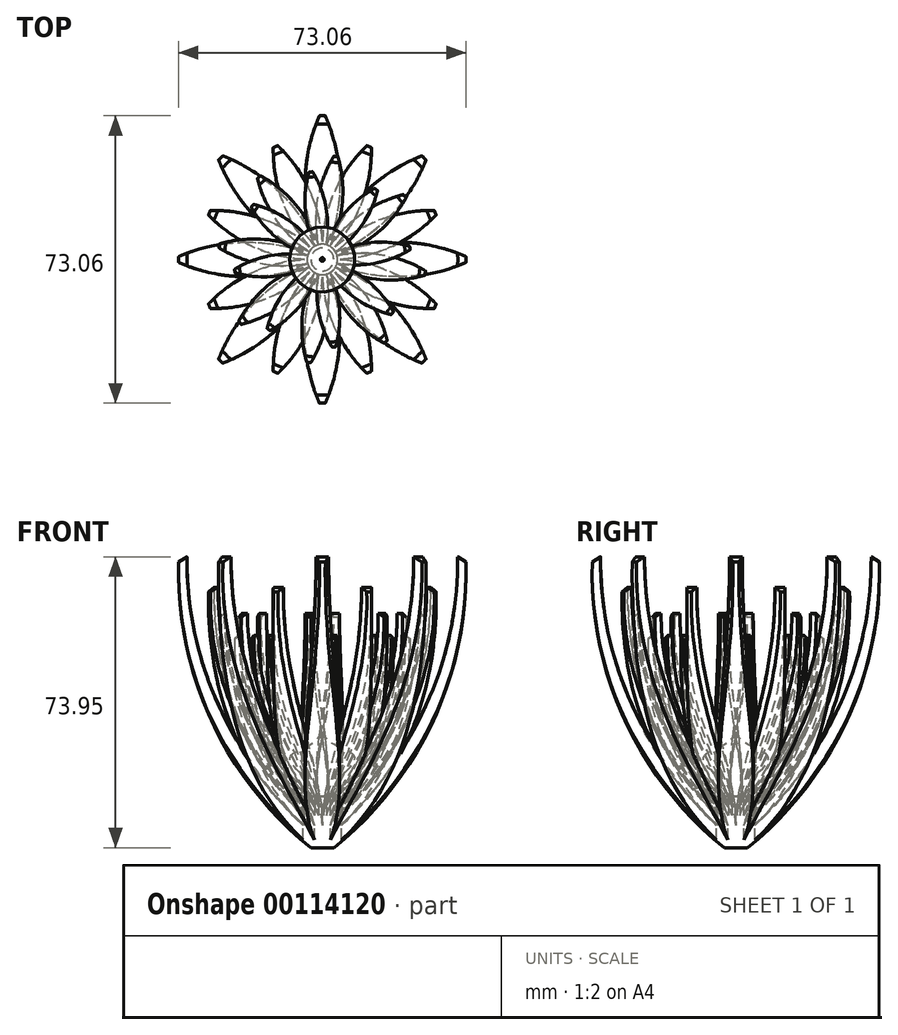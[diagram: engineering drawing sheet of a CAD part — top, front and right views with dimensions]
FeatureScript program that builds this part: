
annotation { "Feature Type Name" : "Feature", "Feature Type Description" : "" }
export const myFeature = defineFeature(function(context is Context, id is Id, definition is map)
    precondition{}
    {
        {
            var Q0;
            Q0=qCreatedBy(makeId("Top.planeOp"),FACE);
            var sketch = newSketch(context, id + "F0", { "sketchPlane" : qUnion([Q0])});
            skLineSegment(sketch, "E0.bottom", {"start": v(38.1, -38.1) * mm, "end": v(-38.1, -38.1) * mm});
            skLineSegment(sketch, "E0.top", {"start": v(38.1, 38.1) * mm, "end": v(-38.1, 38.1) * mm});
            skLineSegment(sketch, "E0.left", {"start": v(38.1, -38.1) * mm, "end": v(38.1, 38.1) * mm});
            skLineSegment(sketch, "E0.right", {"start": v(-38.1, -38.1) * mm, "end": v(-38.1, 38.1) * mm});
            skPoint(sketch, "E0.middle", {"position": v(0, 0) * mm});
            skSolve(sketch);
        }
        {
            var Q0;
            Q0=qSketchRegion(id+"F0",true);
            extrude(context, id + "F1", {"entities" : qUnion([Q0]), "depth" : 76.2 * mm});
        }
        {
            var Q0;
            Q0=makeQuery(id+"F1.opExtrude","CAP_FACE",FACE,{"disambiguationData":[OSD([sQuery(id+"F0.wireOp",EDGE,"E0.bottom"),sQuery(id+"F0.wireOp",EDGE,"E0.top"),sQuery(id+"F0.wireOp",EDGE,"E0.left"),sQuery(id+"F0.wireOp",EDGE,"E0.right")])],"isStart":false});
            var sketch = newSketch(context, id + "F2", { "sketchPlane" : qUnion([Q0])});
            skCircle(sketch, "E1", {"center": v(0, 0) * mm, "radius": 3.18 * mm, "construction": true});
            skLineSegment(sketch, "E2", {"start": v(-38.1, 38.1) * mm, "end": v(38.1, -38.1) * mm, "construction": true});
            skLineSegment(sketch, "E3", {"start": v(38.1, 38.1) * mm, "end": v(-38.1, -38.1) * mm, "construction": true});
            skLineSegment(sketch, "E4", {"start": v(0, -38.1) * mm, "end": v(0, 38.1) * mm, "construction": true});
            skLineSegment(sketch, "E5", {"start": v(-38.1, 0) * mm, "end": v(38.1, 0) * mm, "construction": true});
            skLineSegment(sketch, "E6.bottom", {"start": v(-38.1, 38.1) * mm, "end": v(38.1, 38.1) * mm});
            skLineSegment(sketch, "E6.top", {"start": v(-38.1, -38.1) * mm, "end": v(38.1, -38.1) * mm});
            skLineSegment(sketch, "E6.left", {"start": v(-38.1, 38.1) * mm, "end": v(-38.1, -38.1) * mm});
            skLineSegment(sketch, "E6.right", {"start": v(38.1, 38.1) * mm, "end": v(38.1, -38.1) * mm});
            skArc(sketch, "E7", {"start": v(0, 0) * mm, "mid": v(4.4, 19.05) * mm, "end": v(0, 38.1) * mm});
            skArc(sketch, "E8.MirrorCS", {"start": v(0, 0) * mm, "mid": v(-4.4, 19.05) * mm, "end": v(0, 38.1) * mm});
            skArc(sketch, "E9.1.0", {"start": v(0, 0) * mm, "mid": v(-10.36, 16.58) * mm, "end": v(-26.94, 26.94) * mm});
            skArc(sketch, "E9.1.1", {"start": v(0, 0) * mm, "mid": v(-16.58, 10.36) * mm, "end": v(-26.94, 26.94) * mm});
            skArc(sketch, "E9.2.0", {"start": v(0, 0) * mm, "mid": v(-19.05, 4.4) * mm, "end": v(-38.1, 0) * mm});
            skArc(sketch, "E9.2.1", {"start": v(0, 0) * mm, "mid": v(-19.05, -4.4) * mm, "end": v(-38.1, 0) * mm});
            skArc(sketch, "E9.3.0", {"start": v(0, 0) * mm, "mid": v(-16.58, -10.36) * mm, "end": v(-26.94, -26.94) * mm});
            skArc(sketch, "E9.3.1", {"start": v(0, 0) * mm, "mid": v(-10.36, -16.58) * mm, "end": v(-26.94, -26.94) * mm});
            skArc(sketch, "E9.4.0", {"start": v(0, 0) * mm, "mid": v(-4.4, -19.05) * mm, "end": v(0, -38.1) * mm});
            skArc(sketch, "E9.4.1", {"start": v(0, 0) * mm, "mid": v(4.4, -19.05) * mm, "end": v(0, -38.1) * mm});
            skArc(sketch, "E9.5.0", {"start": v(0, 0) * mm, "mid": v(10.36, -16.58) * mm, "end": v(26.94, -26.94) * mm});
            skArc(sketch, "E9.5.1", {"start": v(0, 0) * mm, "mid": v(16.58, -10.36) * mm, "end": v(26.94, -26.94) * mm});
            skArc(sketch, "E9.6.0", {"start": v(0, 0) * mm, "mid": v(19.05, -4.4) * mm, "end": v(38.1, 0) * mm});
            skArc(sketch, "E9.6.1", {"start": v(0, 0) * mm, "mid": v(19.05, 4.4) * mm, "end": v(38.1, 0) * mm});
            skArc(sketch, "E9.7.0", {"start": v(0, 0) * mm, "mid": v(16.58, 10.36) * mm, "end": v(26.94, 26.94) * mm});
            skArc(sketch, "E9.7.1", {"start": v(0, 0) * mm, "mid": v(10.36, 16.58) * mm, "end": v(26.94, 26.94) * mm});
            skSolve(sketch);
        }
        {
            var Q0;
            {var subQ0=sQuery(id+"F2.wireOp",EDGE,"E9.1.1");var subQ1=sQuery(id+"F2.wireOp",EDGE,"E9.1.0");var subQ2=makeQuery(id+"F2.imprint","INTERSECT",VERTEX,{"derivedFrom":[subQ1,subQ0]});Q0=makeQuery(id+"F2.imprint","IMPRINT",FACE,{"disambiguationData":[TD([[makeQuery(id+"F2.imprint","IMPRINT",EDGE,{"disambiguationData":[TD([[subQ2,1.0]])],"derivedFrom":subQ1}),-1.0]])]});}
            var Q1;
            {var subQ0=sQuery(id+"F2.wireOp",EDGE,"E9.5.1");var subQ1=sQuery(id+"F2.wireOp",EDGE,"E9.5.0");var subQ2=makeQuery(id+"F2.imprint","INTERSECT",VERTEX,{"derivedFrom":[subQ1,subQ0]});Q1=makeQuery(id+"F2.imprint","IMPRINT",FACE,{"disambiguationData":[TD([[makeQuery(id+"F2.imprint","IMPRINT",EDGE,{"disambiguationData":[TD([[subQ2,1.0]])],"derivedFrom":subQ1}),-1.0]])]});}
            var Q2;
            {var subQ0=sQuery(id+"F2.wireOp",EDGE,"E9.3.1");var subQ1=sQuery(id+"F2.wireOp",EDGE,"E9.3.0");var subQ2=makeQuery(id+"F2.imprint","INTERSECT",VERTEX,{"derivedFrom":[subQ1,subQ0]});Q2=makeQuery(id+"F2.imprint","IMPRINT",FACE,{"disambiguationData":[TD([[makeQuery(id+"F2.imprint","IMPRINT",EDGE,{"disambiguationData":[TD([[subQ2,1.0]])],"derivedFrom":subQ1}),-1.0]])]});}
            var Q3;
            {var subQ3=sQuery(id+"F2.wireOp",EDGE,"E9.7.0");var subQ9=sQuery(id+"F2.wireOp",EDGE,"E9.7.1");var subQ11=makeQuery(id+"F2.imprint","INTERSECT",VERTEX,{"derivedFrom":[subQ3,subQ9]});Q3=makeQuery(id+"F2.imprint","IMPRINT",FACE,{"disambiguationData":[TD([[makeQuery(id+"F2.imprint","IMPRINT",EDGE,{"disambiguationData":[TD([[subQ11,1.0]])],"derivedFrom":subQ3}),-1.0]])]});}
            extrude(context, id + "F3", {"entities" : qUnion([Q0, Q1, Q2, Q3]), "operationType" : NewBodyOperationType.REMOVE, "endBound" : BoundingType.THROUGH_ALL, "oppositeDirection" : true, "depth" : 25.4 * mm});
        }
        {
            var Q0;
            Q0=qCreatedBy(makeId("Front.planeOp"),FACE);
            var sketch = newSketch(context, id + "F4", { "sketchPlane" : qUnion([Q0])});
            skLineSegment(sketch, "E10", {"start": v(0, 0) * mm, "end": v(0, 59.45) * mm, "construction": true});
            skPoint(sketch, "E11.0", {"position": v(-38.1, 76.2) * mm});
            skPoint(sketch, "E11.1", {"position": v(38.1, 76.2) * mm});
            skPoint(sketch, "E11.2", {"position": v(38.1, 0) * mm});
            skPoint(sketch, "E11.3", {"position": v(-38.1, 0) * mm});
            skLineSegment(sketch, "E12.bottom", {"start": v(-38.1, 76.2) * mm, "end": v(38.1, 76.2) * mm, "construction": true});
            skLineSegment(sketch, "E12.top", {"start": v(-38.1, 0) * mm, "end": v(38.1, 0) * mm, "construction": true});
            skLineSegment(sketch, "E12.left", {"start": v(-38.1, 76.2) * mm, "end": v(-38.1, 0) * mm, "construction": true});
            skLineSegment(sketch, "E12.right", {"start": v(38.1, 76.2) * mm, "end": v(38.1, 0) * mm, "construction": true});
            skArc(sketch, "E13", {"start": v(-34.42, 76.2) * mm, "mid": v(-25.55, 36.17) * mm, "end": v(0, 4.1) * mm});
            skArc(sketch, "E14", {"start": v(-36.5, 74.86) * mm, "mid": v(-27.42, 32.96) * mm, "end": v(0, 0) * mm});
            skLineSegment(sketch, "E15.bottom", {"start": v(0, 86.56) * mm, "end": v(-47.12, 86.56) * mm});
            skLineSegment(sketch, "E15.top", {"start": v(0, -8.54) * mm, "end": v(-47.12, -8.54) * mm});
            skLineSegment(sketch, "E15.left", {"start": v(0, 86.56) * mm, "end": v(0, -8.54) * mm});
            skLineSegment(sketch, "E15.right", {"start": v(-47.12, 86.56) * mm, "end": v(-47.12, -8.54) * mm});
            skLineSegment(sketch, "E16", {"start": v(-34.42, 76.2) * mm, "end": v(-36.5, 74.86) * mm});
            skLineSegment(sketch, "E17", {"start": v(0, 4.1) * mm, "end": v(0, 0) * mm});
            skSolve(sketch);
        }
        {
            var Q0;
            {var subQ4=sQuery(id+"F4.wireOp",EDGE,"E13");Q0=makeQuery(id+"F4.imprint","IMPRINT",FACE,{"disambiguationData":[TD([[makeQuery(id+"F4.imprint","IMPRINT",EDGE,{"derivedFrom":subQ4}),1.0]])]});}
            var Q1;
            Q1=sQuery(id+"F4.wireOp",EDGE,"E15.left");
            revolve(context, id + "F5", {"operationType" : NewBodyOperationType.REMOVE, "entities" : qUnion([Q0]), "axis" : qUnion([Q1]), "revolveType" : RevolveType.FULL, "oppositeDirection" : true});
        }
        {
            var Q0;
            Q0=qCreatedBy(makeId("Front.planeOp"),FACE);
            var sketch = newSketch(context, id + "F6", { "sketchPlane" : qUnion([Q0])});
            skLineSegment(sketch, "E18", {"start": v(0, 0) * mm, "end": v(0, 66.84) * mm, "construction": true});
            skSolve(sketch);
        }
        {
            var Q0;
            Q0=makeQuery(id+"F1.opExtrude","SWEPT_BODY",BODY,{"disambiguationData":[OSD([sQuery(id+"F0.wireOp",EDGE,"E0.bottom"),sQuery(id+"F0.wireOp",EDGE,"E0.top"),sQuery(id+"F0.wireOp",EDGE,"E0.left"),sQuery(id+"F0.wireOp",EDGE,"E0.right")])]});
            transform(context, id + "F7", {"entities" : qUnion([Q0]), "transformType" : TransformType.TRANSLATION_3D, "dx" : 0 * mm, "dy" : 0 * mm, "dz" : 4.32 * mm, "makeCopy" : true});
        }
        {
            var Q0;
            Q0=makeQuery(id+"F7.opPattern","COPY",BODY,{"derivedFrom":makeQuery(id+"F1.opExtrude","SWEPT_BODY",BODY,{"disambiguationData":[OSD([sQuery(id+"F0.wireOp",EDGE,"E0.bottom"),sQuery(id+"F0.wireOp",EDGE,"E0.top"),sQuery(id+"F0.wireOp",EDGE,"E0.left"),sQuery(id+"F0.wireOp",EDGE,"E0.right")])]}),"instanceName":"1"});
            var Q1;
            Q1=sQuery(id+"F6.wireOp",EDGE,"E18");
            transform(context, id + "F8", {"entities" : qUnion([Q0]), "transformType" : TransformType.ROTATION, "transformAxis" : qUnion([Q1]), "angle" : 22.5 * degree, "makeCopy" : false});
        }
        {
            var Q0;
            Q0=makeQuery(id+"F7.opPattern","COPY",BODY,{"derivedFrom":makeQuery(id+"F1.opExtrude","SWEPT_BODY",BODY,{"disambiguationData":[OSD([sQuery(id+"F0.wireOp",EDGE,"E0.bottom"),sQuery(id+"F0.wireOp",EDGE,"E0.top"),sQuery(id+"F0.wireOp",EDGE,"E0.left"),sQuery(id+"F0.wireOp",EDGE,"E0.right")])]}),"instanceName":"1"});
            var Q1;
            Q1=qCreatedBy(makeId("Origin.pointOp"),VERTEX);
            transform(context, id + "F9", {"entities" : qUnion([Q0]), "transformType" : TransformType.SCALE_UNIFORMLY, "scale" : .85, "scalePoint" : qUnion([Q1]), "makeCopy" : false});
        }
        {
            var Q0;
            Q0=makeQuery(id+"F7.opPattern","COPY",BODY,{"derivedFrom":makeQuery(id+"F1.opExtrude","SWEPT_BODY",BODY,{"disambiguationData":[OSD([sQuery(id+"F0.wireOp",EDGE,"E0.bottom"),sQuery(id+"F0.wireOp",EDGE,"E0.top"),sQuery(id+"F0.wireOp",EDGE,"E0.left"),sQuery(id+"F0.wireOp",EDGE,"E0.right")])]}),"instanceName":"1"});
            transform(context, id + "F10", {"entities" : qUnion([Q0]), "transformType" : TransformType.TRANSLATION_3D, "dx" : 0 * mm, "dy" : 0 * mm, "dz" : 4.32 * mm, "makeCopy" : true});
        }
        {
            var Q0;
            Q0=makeQuery(id+"F10.opPattern","COPY",BODY,{"derivedFrom":makeQuery(id+"F7.opPattern","COPY",BODY,{"derivedFrom":makeQuery(id+"F1.opExtrude","SWEPT_BODY",BODY,{"disambiguationData":[OSD([sQuery(id+"F0.wireOp",EDGE,"E0.bottom"),sQuery(id+"F0.wireOp",EDGE,"E0.top"),sQuery(id+"F0.wireOp",EDGE,"E0.left"),sQuery(id+"F0.wireOp",EDGE,"E0.right")])]}),"instanceName":"1"}),"instanceName":"1"});
            var Q1;
            Q1=sQuery(id+"F6.wireOp",EDGE,"E18");
            transform(context, id + "F11", {"entities" : qUnion([Q0]), "transformType" : TransformType.ROTATION, "transformAxis" : qUnion([Q1]), "angle" : 60 * degree, "makeCopy" : false});
        }
        {
            var Q0;
            Q0=makeQuery(id+"F10.opPattern","COPY",BODY,{"derivedFrom":makeQuery(id+"F7.opPattern","COPY",BODY,{"derivedFrom":makeQuery(id+"F1.opExtrude","SWEPT_BODY",BODY,{"disambiguationData":[OSD([sQuery(id+"F0.wireOp",EDGE,"E0.bottom"),sQuery(id+"F0.wireOp",EDGE,"E0.top"),sQuery(id+"F0.wireOp",EDGE,"E0.left"),sQuery(id+"F0.wireOp",EDGE,"E0.right")])]}),"instanceName":"1"}),"instanceName":"1"});
            var Q1;
            Q1=sQuery(id+"F6.wireOp",VERTEX,"E18.start");
            transform(context, id + "F12", {"entities" : qUnion([Q0]), "transformType" : TransformType.SCALE_UNIFORMLY, "scale" : .85, "scalePoint" : qUnion([Q1]), "makeCopy" : false});
        }
        {
            var Q0;
            Q0=makeQuery(id+"F10.opPattern","COPY",BODY,{"derivedFrom":makeQuery(id+"F7.opPattern","COPY",BODY,{"derivedFrom":makeQuery(id+"F1.opExtrude","SWEPT_BODY",BODY,{"disambiguationData":[OSD([sQuery(id+"F0.wireOp",EDGE,"E0.bottom"),sQuery(id+"F0.wireOp",EDGE,"E0.top"),sQuery(id+"F0.wireOp",EDGE,"E0.left"),sQuery(id+"F0.wireOp",EDGE,"E0.right")])]}),"instanceName":"1"}),"instanceName":"1"});
            transform(context, id + "F13", {"entities" : qUnion([Q0]), "transformType" : TransformType.TRANSLATION_3D, "dx" : 0 * mm, "dy" : 0 * mm, "dz" : 4.32 * mm, "makeCopy" : true});
        }
        {
            var Q0;
            Q0=makeQuery(id+"F13.opPattern","COPY",BODY,{"derivedFrom":makeQuery(id+"F10.opPattern","COPY",BODY,{"derivedFrom":makeQuery(id+"F7.opPattern","COPY",BODY,{"derivedFrom":makeQuery(id+"F1.opExtrude","SWEPT_BODY",BODY,{"disambiguationData":[OSD([sQuery(id+"F0.wireOp",EDGE,"E0.bottom"),sQuery(id+"F0.wireOp",EDGE,"E0.top"),sQuery(id+"F0.wireOp",EDGE,"E0.left"),sQuery(id+"F0.wireOp",EDGE,"E0.right")])]}),"instanceName":"1"}),"instanceName":"1"}),"instanceName":"1"});
            var Q1;
            Q1=sQuery(id+"F6.wireOp",EDGE,"E18");
            transform(context, id + "F14", {"entities" : qUnion([Q0]), "transformType" : TransformType.ROTATION, "transformAxis" : qUnion([Q1]), "angle" : 60 * degree, "makeCopy" : false});
        }
        {
            var Q0;
            Q0=makeQuery(id+"F13.opPattern","COPY",BODY,{"derivedFrom":makeQuery(id+"F10.opPattern","COPY",BODY,{"derivedFrom":makeQuery(id+"F7.opPattern","COPY",BODY,{"derivedFrom":makeQuery(id+"F1.opExtrude","SWEPT_BODY",BODY,{"disambiguationData":[OSD([sQuery(id+"F0.wireOp",EDGE,"E0.bottom"),sQuery(id+"F0.wireOp",EDGE,"E0.top"),sQuery(id+"F0.wireOp",EDGE,"E0.left"),sQuery(id+"F0.wireOp",EDGE,"E0.right")])]}),"instanceName":"1"}),"instanceName":"1"}),"instanceName":"1"});
            var Q1;
            Q1=sQuery(id+"F6.wireOp",VERTEX,"E18.start");
            transform(context, id + "F15", {"entities" : qUnion([Q0]), "transformType" : TransformType.SCALE_UNIFORMLY, "scale" : .85, "scalePoint" : qUnion([Q1]), "makeCopy" : false});
        }
        {
            var Q0;
            Q0=qCreatedBy(makeId("Front.planeOp"),FACE);
            var sketch = newSketch(context, id + "F16", { "sketchPlane" : qUnion([Q0])});
            skLineSegment(sketch, "E19", {"start": v(-0.45, 31.16) * mm, "end": v(-0.45, 15.6) * mm, "construction": true});
            skFitSpline(sketch, "E20", {"points": [v(0, 15.09) * mm, v(-8.18, 25.4) * mm, v(-0.45, 31.16) * mm], "startDerivative": vector(-17.53, 26.01) * mm, "endDerivative": vector(7.37, 21.07) * mm});
            skLineSegment(sketch, "E21", {"start": v(0, 15.09) * mm, "end": v(0, 31.16) * mm});
            skLineSegment(sketch, "E22", {"start": v(-0.45, 31.16) * mm, "end": v(-0.3, 31.16) * mm});
            skArc(sketch, "E23", {"start": v(-0.3, 31.16) * mm, "mid": v(-0.22, 30.89) * mm, "end": v(0, 30.71) * mm});
            skLineSegment(sketch, "E24", {"start": v(-3.87, 20.53) * mm, "end": v(-3.87, 3.85) * mm});
            skLineSegment(sketch, "E25", {"start": v(-3.87, 3.85) * mm, "end": v(0, 3.85) * mm});
            skLineSegment(sketch, "E26", {"start": v(0, 3.85) * mm, "end": v(0, 18.29) * mm});
            skSolve(sketch);
        }
        {
            var Q0;
            Q0=qSketchRegion(id+"F16",true);
            var Q1;
            Q1=sQuery(id+"F16.wireOp",EDGE,"E21");
            revolve(context, id + "F17", {"operationType" : NewBodyOperationType.ADD, "entities" : qUnion([Q0]), "axis" : qUnion([Q1]), "revolveType" : RevolveType.FULL});
        }
        {
            var Q0;
            Q0=qCreatedBy(makeId("Top.planeOp"),FACE);
            var sketch = newSketch(context, id + "F18", { "sketchPlane" : qUnion([Q0])});
            skCircle(sketch, "E27", {"center": v(0, 0) * mm, "radius": 6.35 * mm});
            skSolve(sketch);
        }
        {
            var Q0;
            Q0=makeQuery(id+"F17.opRevolve","SWEPT_EDGE",EDGE,{"disambiguationData":[OSD([sQuery(id+"F16.wireOp",EDGE,"E20"),sQuery(id+"F16.wireOp",EDGE,"E24")])]});
            fillet(context, id + "F19", {"entities" : qUnion([Q0]), "radius" : 5.08 * mm, "tangentPropagation" : true, "allowEdgeOverflow" : false});
        }
        {
            var Q0;
            Q0=qSketchRegion(id+"F18",true);
            extrude(context, id + "F20", {"entities" : qUnion([Q0]), "operationType" : NewBodyOperationType.REMOVE, "depth" : 2.25 * mm});
        }
    });
